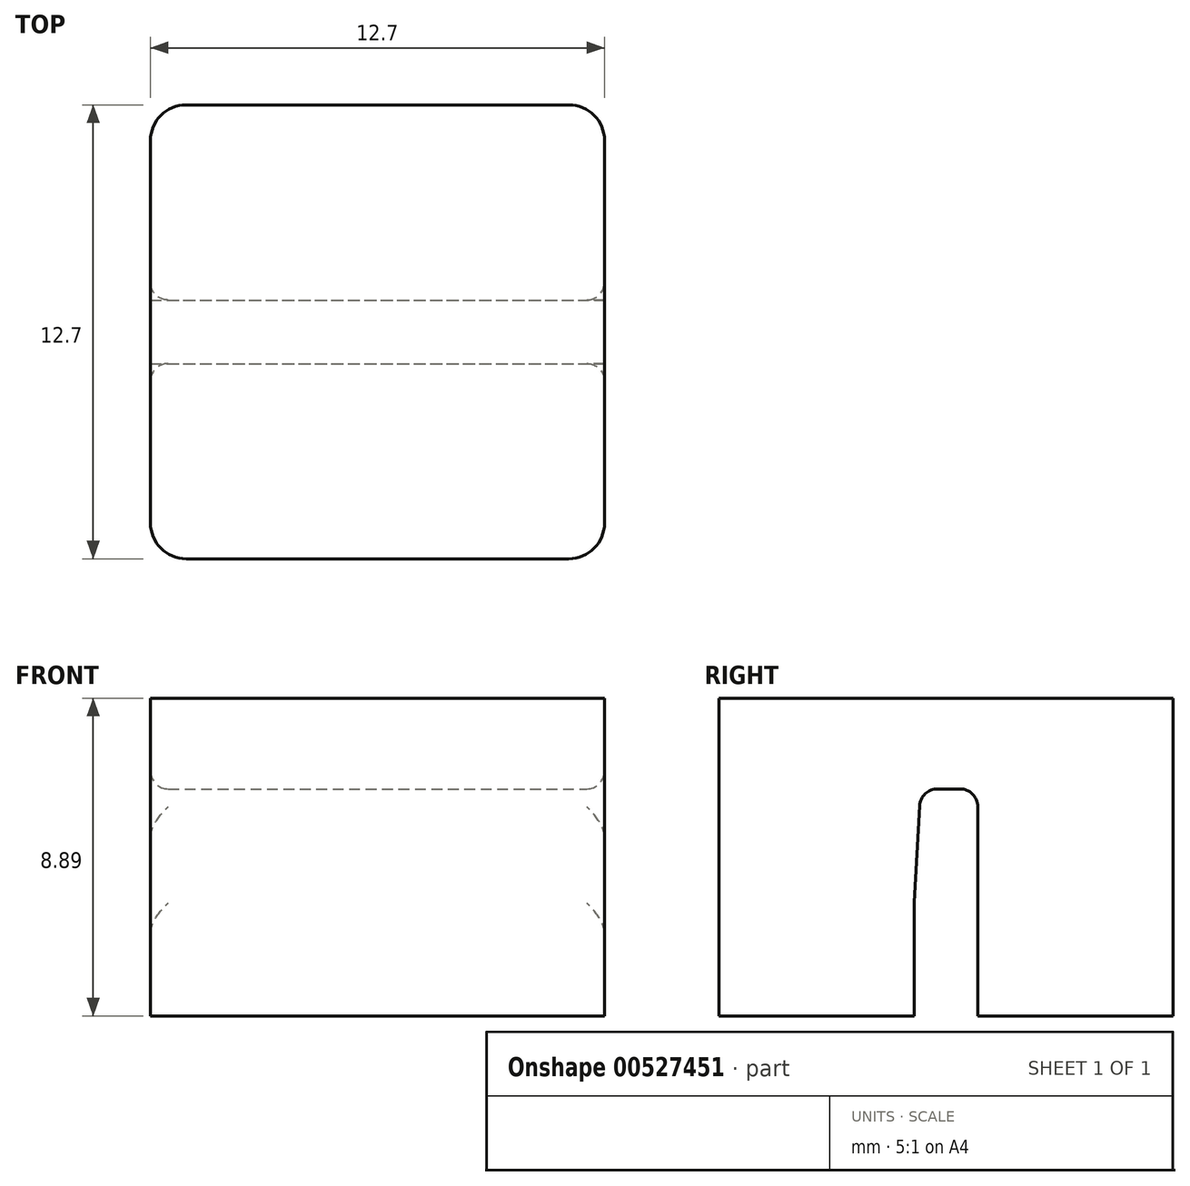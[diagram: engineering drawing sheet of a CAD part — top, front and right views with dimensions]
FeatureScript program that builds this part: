
annotation { "Feature Type Name" : "Feature", "Feature Type Description" : "" }
export const myFeature = defineFeature(function(context is Context, id is Id, definition is map)
    precondition{}
    {
        {
            var Q0;
            Q0=qCreatedBy(makeId("Top.planeOp"),FACE);
            var sketch = newSketch(context, id + "F0", { "sketchPlane" : qUnion([Q0])});
            skLineSegment(sketch, "E0.bottom", {"start": v(6.35, -6.35) * mm, "end": v(-6.35, -6.35) * mm});
            skLineSegment(sketch, "E0.top", {"start": v(6.35, 6.35) * mm, "end": v(-6.35, 6.35) * mm});
            skLineSegment(sketch, "E0.left", {"start": v(6.35, -6.35) * mm, "end": v(6.35, 6.35) * mm});
            skLineSegment(sketch, "E0.right", {"start": v(-6.35, -6.35) * mm, "end": v(-6.35, 6.35) * mm});
            skPoint(sketch, "E0.middle", {"position": v(0, 0) * mm});
            skSolve(sketch);
        }
        {
            var Q0;
            Q0=makeQuery(id+"F0.imprint","IMPRINT",FACE,{"disambiguationData":[TD([[makeQuery(id+"F0.imprint","IMPRINT",EDGE,{"derivedFrom":sQuery(id+"F0.wireOp",EDGE,"E0.bottom")}),-1.0]])]});
            extrude(context, id + "F1", {"entities" : qUnion([Q0]), "depth" : 15.24 * mm, "offsetDistance" : 25 * mm});
        }
        {
            var Q0;
            Q0=makeQuery(id+"F1.opExtrude","SWEPT_FACE",FACE,{"disambiguationData":[OSD([sQuery(id+"F0.wireOp",EDGE,"E0.left")])]});
            var sketch = newSketch(context, id + "F2", { "sketchPlane" : qUnion([Q0])});
            skLineSegment(sketch, "E1.bottom", {"start": v(0.89, 0) * mm, "end": v(-0.89, 0) * mm});
            skLineSegment(sketch, "E1.top", {"start": v(0.89, 6.35) * mm, "end": v(-0.89, 6.35) * mm});
            skLineSegment(sketch, "E1.left", {"start": v(0.89, 0) * mm, "end": v(0.89, 6.35) * mm});
            skLineSegment(sketch, "E1.right", {"start": v(-0.89, 0) * mm, "end": v(-0.89, 6.35) * mm});
            skPoint(sketch, "E1.middle", {"position": v(0, 3.17) * mm});
            skSolve(sketch);
        }
        {
            var Q0;
            Q0=makeQuery(id+"F2.imprint","IMPRINT",FACE,{"disambiguationData":[TD([[makeQuery(id+"F2.imprint","IMPRINT",EDGE,{"derivedFrom":sQuery(id+"F2.wireOp",EDGE,"E1.bottom")}),1.0]])]});
            extrude(context, id + "F3", {"entities" : qUnion([Q0]), "operationType" : NewBodyOperationType.REMOVE, "oppositeDirection" : true, "depth" : 25 * mm, "offsetDistance" : 25 * mm});
        }
        {
            var Q0;
            Q0=makeQuery(id+"F1.opExtrude","SWEPT_FACE",FACE,{"disambiguationData":[OSD([sQuery(id+"F0.wireOp",EDGE,"E0.left")])]});
            var sketch = newSketch(context, id + "F4", { "sketchPlane" : qUnion([Q0])});
            skLineSegment(sketch, "E2", {"start": v(-0.89, 3.17) * mm, "end": v(-0.7, 6.35) * mm});
            skLineSegment(sketch, "E3", {"start": v(-0.7, 6.35) * mm, "end": v(-0.89, 6.35) * mm});
            skLineSegment(sketch, "E4", {"start": v(-0.89, 6.35) * mm, "end": v(-0.89, 3.17) * mm});
            skSolve(sketch);
        }
        {
            var Q0;
            Q0=makeQuery(id+"F4.imprint","IMPRINT",FACE,{"disambiguationData":[TD([[makeQuery(id+"F4.imprint","IMPRINT",EDGE,{"derivedFrom":sQuery(id+"F4.wireOp",EDGE,"E2")}),1.0]])]});
            var Q1;
            Q1=makeQuery(id+"F1.opExtrude","SWEPT_FACE",FACE,{"disambiguationData":[OSD([sQuery(id+"F0.wireOp",EDGE,"E0.right")])]});
            extrude(context, id + "F5", {"entities" : qUnion([Q0]), "operationType" : NewBodyOperationType.ADD, "endBound" : BoundingType.UP_TO_SURFACE, "oppositeDirection" : true, "depth" : 25 * mm, "endBoundEntityFace" : qUnion([Q1]), "offsetDistance" : 25 * mm});
        }
        {
            var Q0;
            Q0=makeQuery(id+"F1.opExtrude","SWEPT_EDGE",EDGE,{"disambiguationData":[OSD([sQuery(id+"F0.wireOp",EDGE,"E0.bottom"),sQuery(id+"F0.wireOp",EDGE,"E0.left")])]});
            var Q1;
            Q1=makeQuery(id+"F1.opExtrude","SWEPT_EDGE",EDGE,{"disambiguationData":[OSD([sQuery(id+"F0.wireOp",EDGE,"E0.bottom"),sQuery(id+"F0.wireOp",EDGE,"E0.right")])]});
            var Q2;
            Q2=makeQuery(id+"F1.opExtrude","SWEPT_EDGE",EDGE,{"disambiguationData":[OSD([sQuery(id+"F0.wireOp",EDGE,"E0.top"),sQuery(id+"F0.wireOp",EDGE,"E0.right")])]});
            var Q3;
            Q3=makeQuery(id+"F1.opExtrude","SWEPT_EDGE",EDGE,{"disambiguationData":[OSD([sQuery(id+"F0.wireOp",EDGE,"E0.top"),sQuery(id+"F0.wireOp",EDGE,"E0.left")])]});
            fillet(context, id + "F6", {"entities" : qUnion([Q0, Q1, Q2, Q3]), "radius" : 1 * mm, "tangentPropagation" : true, "allowEdgeOverflow" : false});
        }
        {
            var Q0;
            Q0=makeQuery(id+"F3.boolean.opBoolean","COPY",FACE,{"derivedFrom":makeQuery(id+"F3.opExtrude","SWEPT_FACE",FACE,{"disambiguationData":[OSD([sQuery(id+"F2.wireOp",EDGE,"E1.top")])]})});
            var Q1;
            Q1=makeQuery(id+"F5.opExtrude","SWEPT_FACE",FACE,{"disambiguationData":[OSD([sQuery(id+"F4.wireOp",EDGE,"E2")])]});
            var Q2;
            Q2=makeQuery(id+"FcWPbxFVJ2alZCF_1.1.F5.opExtrude","SWEPT_FACE",FACE,{"disambiguationData":[OSD([sQuery(id+"F4.wireOp",EDGE,"E2")])]});
            fillet(context, id + "F7", {"entities" : qUnion([Q0, Q1, Q2]), "radius" : .5 * mm, "tangentPropagation" : true, "allowEdgeOverflow" : false});
        }
        {
            var Q0;
            Q0=makeQuery(id+"F1.opExtrude","CAP_FACE",FACE,{"disambiguationData":[OSD([sQuery(id+"F0.wireOp",EDGE,"E0.bottom"),sQuery(id+"F0.wireOp",EDGE,"E0.top"),sQuery(id+"F0.wireOp",EDGE,"E0.left"),sQuery(id+"F0.wireOp",EDGE,"E0.right")])],"isStart":false});
            extrude(context, id + "F8", {"entities" : qUnion([Q0]), "operationType" : NewBodyOperationType.REMOVE, "oppositeDirection" : true, "depth" : 6.35 * mm, "offsetDistance" : 25 * mm});
        }
    });
